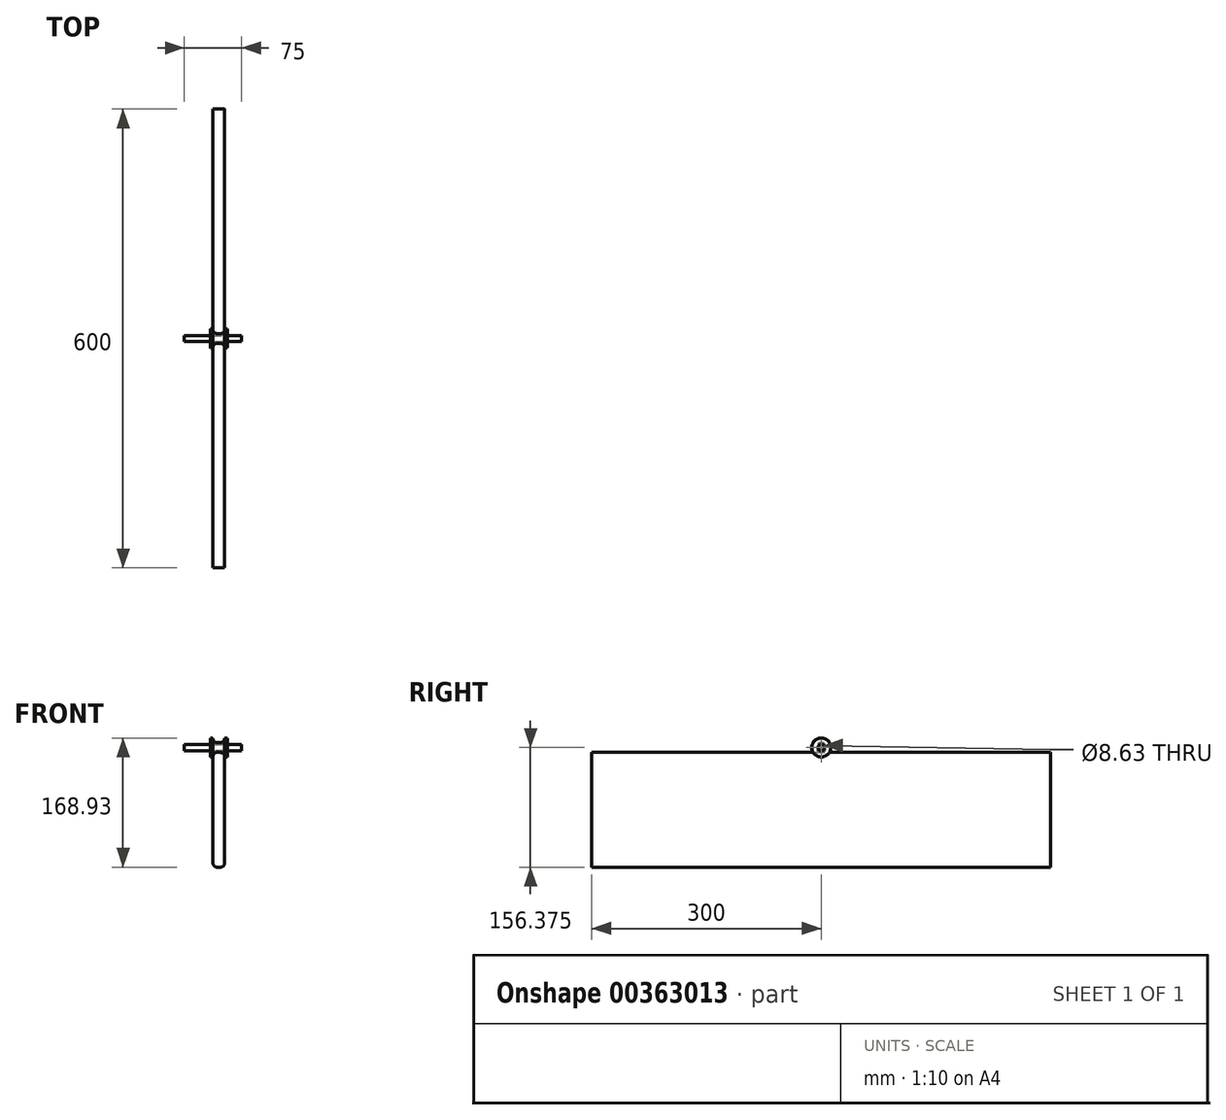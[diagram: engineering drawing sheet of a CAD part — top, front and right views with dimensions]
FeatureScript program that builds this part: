
annotation { "Feature Type Name" : "Feature", "Feature Type Description" : "" }
export const myFeature = defineFeature(function(context is Context, id is Id, definition is map)
    precondition{}
    {
        {
            var Q0;
            Q0=qCreatedBy(makeId("Front.planeOp"),FACE);
            var sketch = newSketch(context, id + "F0", { "sketchPlane" : qUnion([Q0])});
            skLineSegment(sketch, "E0.bottom", {"start": v(-10, 75) * mm, "end": v(-5, 75) * mm});
            skLineSegment(sketch, "E0.top", {"start": v(-10, -75) * mm, "end": v(-5, -75) * mm});
            skLineSegment(sketch, "E0.left", {"start": v(-15, 70) * mm, "end": v(-15, -70) * mm});
            skLineSegment(sketch, "E0.right", {"start": v(0, 70) * mm, "end": v(0, -70) * mm});
            skPoint(sketch, "E1.visualSharp", {"position": v(-15, 75) * mm});
            skArc(sketch, "E1.filletArc", {"start": v(-10, 75) * mm, "mid": v(-13.54, 73.54) * mm, "end": v(-15, 70) * mm});
            skPoint(sketch, "E2.visualSharp", {"position": v(0, 75) * mm});
            skArc(sketch, "E2.filletArc", {"start": v(0, 70) * mm, "mid": v(-1.46, 73.54) * mm, "end": v(-5, 75) * mm});
            skPoint(sketch, "E3.visualSharp", {"position": v(0, -75) * mm});
            skArc(sketch, "E3.filletArc", {"start": v(-5, -75) * mm, "mid": v(-1.46, -73.54) * mm, "end": v(0, -70) * mm});
            skPoint(sketch, "E4.visualSharp", {"position": v(-15, -75) * mm});
            skArc(sketch, "E4.filletArc", {"start": v(-15, -70) * mm, "mid": v(-13.54, -73.54) * mm, "end": v(-10, -75) * mm});
            skSolve(sketch);
        }
        {
            var Q0;
            Q0=makeQuery(id+"F0.imprint","IMPRINT",FACE,{"disambiguationData":[TD([[makeQuery(id+"F0.imprint","IMPRINT",EDGE,{"derivedFrom":sQuery(id+"F0.wireOp",EDGE,"E0.bottom")}),-1.0]])]});
            extrude(context, id + "F1", {"entities" : qUnion([Q0]), "endBound" : BoundingType.SYMMETRIC, "depth" : 600 * mm});
        }
        {
            var Q0;
            Q0=makeQuery(id+"F1.opExtrude","SWEPT_FACE",FACE,{"disambiguationData":[OSD([sQuery(id+"F0.wireOp",EDGE,"E0.left")])]});
            var sketch = newSketch(context, id + "F2", { "sketchPlane" : qUnion([Q0])});
            skCircle(sketch, "E5", {"center": v(0, 81.38) * mm, "radius": 4 * mm});
            skSolve(sketch);
        }
        {
            var Q0;
            Q0 = qSketchRegion(id + "F2", true);
            extrude(context, id + "F3", {"entities" : qUnion([Q0]), "endBound" : BoundingType.SYMMETRIC, "depth" : 75 * mm});
        }
        {
            var Q0;
            Q0=qCreatedBy(makeId("Front.planeOp"),FACE);
            var sketch = newSketch(context, id + "F4", { "sketchPlane" : qUnion([Q0])});
            skLineSegment(sketch, "E6", {"start": v(-18.58, 68.83) * mm, "end": v(-18.58, 77.06) * mm});
            skLineSegment(sketch, "E7", {"start": v(-18.58, 77.06) * mm, "end": v(3.51, 77.06) * mm});
            skLineSegment(sketch, "E8", {"start": v(3.51, 77.06) * mm, "end": v(3.51, 69.06) * mm});
            skLineSegment(sketch, "E9", {"start": v(3.51, 69.06) * mm, "end": v(0, 69.06) * mm});
            skLineSegment(sketch, "E10", {"start": v(0, 69.06) * mm, "end": v(0, 69.9) * mm});
            skLineSegment(sketch, "E11", {"start": v(-5, 74.9) * mm, "end": v(-10.07, 74.9) * mm});
            skLineSegment(sketch, "E12", {"start": v(-15.07, 69.9) * mm, "end": v(-15.07, 69.06) * mm});
            skLineSegment(sketch, "E13", {"start": v(-15.07, 69.06) * mm, "end": v(-18.58, 68.83) * mm});
            skPoint(sketch, "E14.visualSharp", {"position": v(-15.07, 74.9) * mm});
            skArc(sketch, "E14.filletArc", {"start": v(-10.07, 74.9) * mm, "mid": v(-13.6, 73.44) * mm, "end": v(-15.07, 69.9) * mm});
            skPoint(sketch, "E15.visualSharp", {"position": v(0, 74.9) * mm});
            skArc(sketch, "E15.filletArc", {"start": v(0, 69.9) * mm, "mid": v(-1.46, 73.44) * mm, "end": v(-5, 74.9) * mm});
            skSolve(sketch);
        }
        {
            var Q0;
            Q0=makeQuery(id+"F4.imprint","IMPRINT",FACE,{"disambiguationData":[TD([[makeQuery(id+"F4.imprint","IMPRINT",EDGE,{"derivedFrom":sQuery(id+"F4.wireOp",EDGE,"E6")}),-1.0]])]});
            var Q1;
            Q1=makeQuery(id+"F3.opExtrude","SWEPT_FACE",FACE,{"disambiguationData":[OSD([sQuery(id+"F2.wireOp",EDGE,"E5")])]});
            revolve(context, id + "F5", {"entities" : qUnion([Q0]), "axis" : qUnion([Q1]), "revolveType" : RevolveType.FULL});
        }
    });
